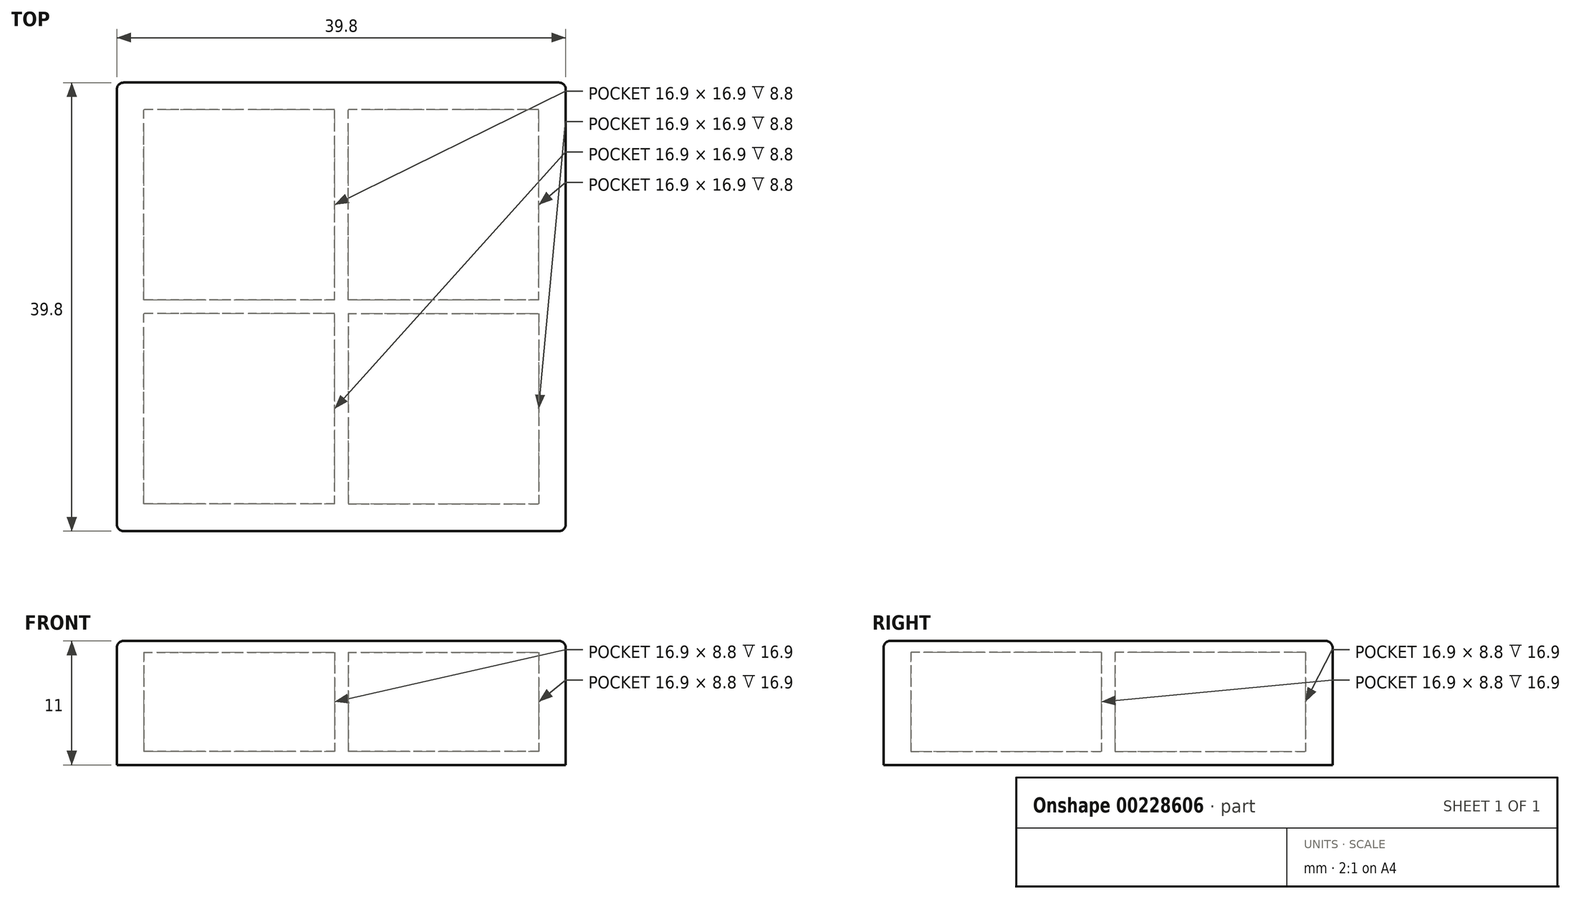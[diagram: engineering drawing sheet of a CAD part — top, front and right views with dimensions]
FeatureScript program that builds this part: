
annotation { "Feature Type Name" : "Feature", "Feature Type Description" : "" }
export const myFeature = defineFeature(function(context is Context, id is Id, definition is map)
    precondition{}
    {
        {
            var Q0;
            Q0=qCreatedBy(makeId("Top.planeOp"),FACE);
            var sketch = newSketch(context, id + "F0", { "sketchPlane" : qUnion([Q0])});
            skLineSegment(sketch, "E0.bottom", {"start": v(-39.8, 57) * mm, "end": v(0, 57) * mm});
            skLineSegment(sketch, "E0.top", {"start": v(-39.8, 17.2) * mm, "end": v(0, 17.2) * mm});
            skLineSegment(sketch, "E0.left", {"start": v(-39.8, 57) * mm, "end": v(-39.8, 17.2) * mm});
            skLineSegment(sketch, "E0.right", {"start": v(0, 57) * mm, "end": v(0, 17.2) * mm});
            skLineSegment(sketch, "E1.0", {"start": v(-38.6, 18.4) * mm, "end": v(-1.2, 18.4) * mm});
            skLineSegment(sketch, "E1.1", {"start": v(-38.6, 55.8) * mm, "end": v(-38.6, 18.4) * mm});
            skLineSegment(sketch, "E1.2", {"start": v(-38.6, 55.8) * mm, "end": v(-1.2, 55.8) * mm});
            skLineSegment(sketch, "E1.3", {"start": v(-1.2, 55.8) * mm, "end": v(-1.2, 18.4) * mm});
            skLineSegment(sketch, "E2.0", {"start": v(-37.4, 54.6) * mm, "end": v(-2.4, 54.6) * mm});
            skLineSegment(sketch, "E2.1", {"start": v(-37.4, 54.6) * mm, "end": v(-37.4, 19.6) * mm});
            skLineSegment(sketch, "E2.2", {"start": v(-37.4, 19.6) * mm, "end": v(-2.4, 19.6) * mm});
            skLineSegment(sketch, "E2.3", {"start": v(-2.4, 54.6) * mm, "end": v(-2.4, 19.6) * mm});
            skLineSegment(sketch, "E3", {"start": v(-19.3, 54.6) * mm, "end": v(-19.3, 37.7) * mm});
            skLineSegment(sketch, "E4", {"start": v(-20.5, 54.6) * mm, "end": v(-20.5, 37.7) * mm});
            skLineSegment(sketch, "E5", {"start": v(-37.4, 37.7) * mm, "end": v(-20.5, 37.7) * mm});
            skLineSegment(sketch, "E6", {"start": v(-37.4, 36.5) * mm, "end": v(-20.5, 36.5) * mm});
            skLineSegment(sketch, "E7", {"start": v(-19.3, 37.7) * mm, "end": v(-2.4, 37.7) * mm});
            skLineSegment(sketch, "E8", {"start": v(-20.5, 36.5) * mm, "end": v(-20.5, 19.6) * mm});
            skLineSegment(sketch, "E9", {"start": v(-19.3, 36.5) * mm, "end": v(-2.4, 36.5) * mm});
            skLineSegment(sketch, "E10", {"start": v(-19.3, 36.5) * mm, "end": v(-19.3, 19.6) * mm});
            skSolve(sketch);
        }
        {
            var Q0;
            Q0=makeQuery(id+"F0.imprint","IMPRINT",FACE,{"disambiguationData":[TD([[makeQuery(id+"F0.imprint","IMPRINT",EDGE,{"derivedFrom":sQuery(id+"F0.wireOp",EDGE,"E0.bottom")}),-1.0]])]});
            var Q1;
            {var subQ3=sQuery(id+"F0.wireOp",EDGE,"E3");Q1=makeQuery(id+"F0.imprint","IMPRINT",FACE,{"disambiguationData":[TD([[makeQuery(id+"F0.imprint","IMPRINT",EDGE,{"derivedFrom":subQ3}),1.0]])]});}
            var Q2;
            {var subQ3=sQuery(id+"F0.wireOp",EDGE,"E6");Q2=makeQuery(id+"F0.imprint","IMPRINT",FACE,{"disambiguationData":[TD([[makeQuery(id+"F0.imprint","IMPRINT",EDGE,{"derivedFrom":subQ3}),-1.0]])]});}
            var Q3;
            {var subQ3=sQuery(id+"F0.wireOp",EDGE,"E4");Q3=makeQuery(id+"F0.imprint","IMPRINT",FACE,{"disambiguationData":[TD([[makeQuery(id+"F0.imprint","IMPRINT",EDGE,{"derivedFrom":subQ3}),-1.0]])]});}
            var Q4;
            {var subQ2=sQuery(id+"F0.wireOp",EDGE,"E3");Q4=makeQuery(id+"F0.imprint","IMPRINT",FACE,{"disambiguationData":[TD([[makeQuery(id+"F0.imprint","IMPRINT",EDGE,{"derivedFrom":subQ2}),-1.0]])]});}
            var Q5;
            Q5=makeQuery(id+"F0.imprint","IMPRINT",FACE,{"disambiguationData":[TD([[makeQuery(id+"F0.imprint","IMPRINT",EDGE,{"derivedFrom":sQuery(id+"F0.wireOp",EDGE,"E1.0")}),1.0]])]});
            var Q6;
            {var subQ4=sQuery(id+"F0.wireOp",EDGE,"E9");Q6=makeQuery(id+"F0.imprint","IMPRINT",FACE,{"disambiguationData":[TD([[makeQuery(id+"F0.imprint","IMPRINT",EDGE,{"derivedFrom":subQ4}),-1.0]])]});}
            extrude(context, id + "F1", {"entities" : qUnion([Q0, Q1, Q2, Q3, Q4, Q5, Q6]), "depth" : 1.2 * mm});
        }
        {
            var Q0;
            {var subQ2=sQuery(id+"F0.wireOp",EDGE,"E3");Q0=makeQuery(id+"F0.imprint","IMPRINT",FACE,{"disambiguationData":[TD([[makeQuery(id+"F0.imprint","IMPRINT",EDGE,{"derivedFrom":subQ2}),-1.0]])]});}
            var Q1;
            Q1=makeQuery(id+"F0.imprint","IMPRINT",FACE,{"disambiguationData":[TD([[makeQuery(id+"F0.imprint","IMPRINT",EDGE,{"derivedFrom":sQuery(id+"F0.wireOp",EDGE,"E1.0")}),1.0]])]});
            var Q2;
            Q2=sQuery(id+"F0.wireOp",EDGE,"E1.1");
            var Q3;
            Q3=sQuery(id+"F0.wireOp",EDGE,"E2.1");
            var Q4;
            Q4=sQuery(id+"F0.wireOp",EDGE,"E1.2");
            var Q5;
            Q5=sQuery(id+"F0.wireOp",EDGE,"E2.0");
            var Q6;
            Q6=sQuery(id+"F0.wireOp",EDGE,"E2.3");
            var Q7;
            Q7=sQuery(id+"F0.wireOp",EDGE,"E1.3");
            var Q8;
            Q8=sQuery(id+"F0.wireOp",EDGE,"E1.0");
            var Q9;
            Q9=sQuery(id+"F0.wireOp",EDGE,"E2.2");
            var Q10;
            Q10=sQuery(id+"F0.wireOp",EDGE,"E10");
            var Q11;
            Q11=sQuery(id+"F0.wireOp",EDGE,"E5");
            var Q12;
            Q12=sQuery(id+"F0.wireOp",EDGE,"E6");
            var Q13;
            Q13=sQuery(id+"F0.wireOp",EDGE,"E8");
            var Q14;
            Q14=sQuery(id+"F0.wireOp",EDGE,"E3");
            var Q15;
            Q15=sQuery(id+"F0.wireOp",EDGE,"E4");
            var Q16;
            Q16=sQuery(id+"F0.wireOp",EDGE,"E7");
            var Q17;
            Q17=sQuery(id+"F0.wireOp",EDGE,"E9");
            extrude(context, id + "F2", {"entities" : qUnion([Q0, Q1]), "operationType" : NewBodyOperationType.ADD, "surfaceEntities" : qUnion([Q2, Q3, Q4, Q5, Q6, Q7, Q8, Q9, Q10, Q11, Q12, Q13, Q14, Q15, Q16, Q17]), "depth" : 10 * mm});
        }
        {
            var Q0;
            Q0 = qSketchRegion(id + "F0", true);
            var Q1;
            Q1=sQuery(id+"F0.wireOp",EDGE,"E0.left");
            var Q2;
            Q2=sQuery(id+"F0.wireOp",EDGE,"E0.bottom");
            var Q3;
            Q3=sQuery(id+"F0.wireOp",EDGE,"E0.top");
            var Q4;
            Q4=sQuery(id+"F0.wireOp",EDGE,"E0.right");
            extrude(context, id + "F3", {"entities" : qUnion([Q0]), "surfaceEntities" : qUnion([Q1, Q2, Q3, Q4]), "depth" : 11 * mm, "hasSecondDirection" : true, "secondDirectionOppositeDirection" : false, "secondDirectionDepth" : 1.2 * mm});
        }
        {
            var Q0;
            Q0 = qSketchRegion(id + "F0", true);
            var Q1;
            {var subQ3=sQuery(id+"F0.wireOp",EDGE,"E4");Q1=makeQuery(id+"F0.imprint","IMPRINT",FACE,{"disambiguationData":[TD([[makeQuery(id+"F0.imprint","IMPRINT",EDGE,{"derivedFrom":subQ3}),-1.0]])]});}
            var Q2;
            {var subQ3=sQuery(id+"F0.wireOp",EDGE,"E3");Q2=makeQuery(id+"F0.imprint","IMPRINT",FACE,{"disambiguationData":[TD([[makeQuery(id+"F0.imprint","IMPRINT",EDGE,{"derivedFrom":subQ3}),1.0]])]});}
            var Q3;
            {var subQ4=sQuery(id+"F0.wireOp",EDGE,"E9");Q3=makeQuery(id+"F0.imprint","IMPRINT",FACE,{"disambiguationData":[TD([[makeQuery(id+"F0.imprint","IMPRINT",EDGE,{"derivedFrom":subQ4}),-1.0]])]});}
            var Q4;
            {var subQ3=sQuery(id+"F0.wireOp",EDGE,"E6");Q4=makeQuery(id+"F0.imprint","IMPRINT",FACE,{"disambiguationData":[TD([[makeQuery(id+"F0.imprint","IMPRINT",EDGE,{"derivedFrom":subQ3}),-1.0]])]});}
            var Q5;
            Q5=makeQuery(id+"F0.imprint","IMPRINT",FACE,{"disambiguationData":[TD([[makeQuery(id+"F0.imprint","IMPRINT",EDGE,{"derivedFrom":sQuery(id+"F0.wireOp",EDGE,"E1.0")}),1.0]])]});
            var Q6;
            {var subQ2=sQuery(id+"F0.wireOp",EDGE,"E3");Q6=makeQuery(id+"F0.imprint","IMPRINT",FACE,{"disambiguationData":[TD([[makeQuery(id+"F0.imprint","IMPRINT",EDGE,{"derivedFrom":subQ2}),-1.0]])]});}
            var Q7;
            Q7=sQuery(id+"F0.wireOp",EDGE,"E0.top");
            var Q8;
            Q8=sQuery(id+"F0.wireOp",EDGE,"E0.right");
            extrude(context, id + "F4", {"entities" : qUnion([Q0, Q1, Q2, Q3, Q4, Q5, Q6]), "operationType" : NewBodyOperationType.ADD, "surfaceEntities" : qUnion([Q7, Q8]), "depth" : 11 * mm, "hasSecondDirection" : true, "secondDirectionOppositeDirection" : false, "secondDirectionDepth" : 10 * mm});
        }
        {
            var Q0;
            {var subQ0=sQuery(id+"F0.wireOp",EDGE,"E0.right");var subQ1=sQuery(id+"F0.wireOp",EDGE,"E0.left");var subQ2=sQuery(id+"F0.wireOp",EDGE,"E0.top");var subQ3=sQuery(id+"F0.wireOp",EDGE,"E0.bottom");Q0=makeQuery(id+"F4.boolean.opBoolean","MERGE",FACE,{"derivedFrom":[makeQuery(id+"F3.opExtrude","CAP_FACE",FACE,{"disambiguationData":[OSD([subQ3,subQ2,subQ1,subQ0,sQuery(id+"F0.wireOp",EDGE,"E1.0"),sQuery(id+"F0.wireOp",EDGE,"E1.1"),sQuery(id+"F0.wireOp",EDGE,"E1.2"),sQuery(id+"F0.wireOp",EDGE,"E1.3")])],"isStart":false}),makeQuery(id+"F4.opExtrude","CAP_FACE",FACE,{"disambiguationData":[OSD([subQ3,subQ2,subQ1,subQ0])],"isStart":false})]});}
            var Q1;
            Q1=makeQuery(id+"F3.opExtrude","SWEPT_EDGE",EDGE,{"disambiguationData":[OSD([sQuery(id+"F0.wireOp",EDGE,"E0.bottom"),sQuery(id+"F0.wireOp",EDGE,"E0.left")])]});
            var Q2;
            Q2=makeQuery(id+"F3.opExtrude","SWEPT_EDGE",EDGE,{"disambiguationData":[OSD([sQuery(id+"F0.wireOp",EDGE,"E0.top"),sQuery(id+"F0.wireOp",EDGE,"E0.left")])]});
            var Q3;
            Q3=makeQuery(id+"F3.opExtrude","SWEPT_EDGE",EDGE,{"disambiguationData":[OSD([sQuery(id+"F0.wireOp",EDGE,"E0.top"),sQuery(id+"F0.wireOp",EDGE,"E0.right")])]});
            var Q4;
            Q4=makeQuery(id+"F3.opExtrude","SWEPT_EDGE",EDGE,{"disambiguationData":[OSD([sQuery(id+"F0.wireOp",EDGE,"E0.bottom"),sQuery(id+"F0.wireOp",EDGE,"E0.right")])]});
            fillet(context, id + "F5", {"entities" : qUnion([Q0, Q1, Q2, Q3, Q4]), "radius" : 0.6 * mm, "tangentPropagation" : true, "allowEdgeOverflow" : false});
        }
    });
